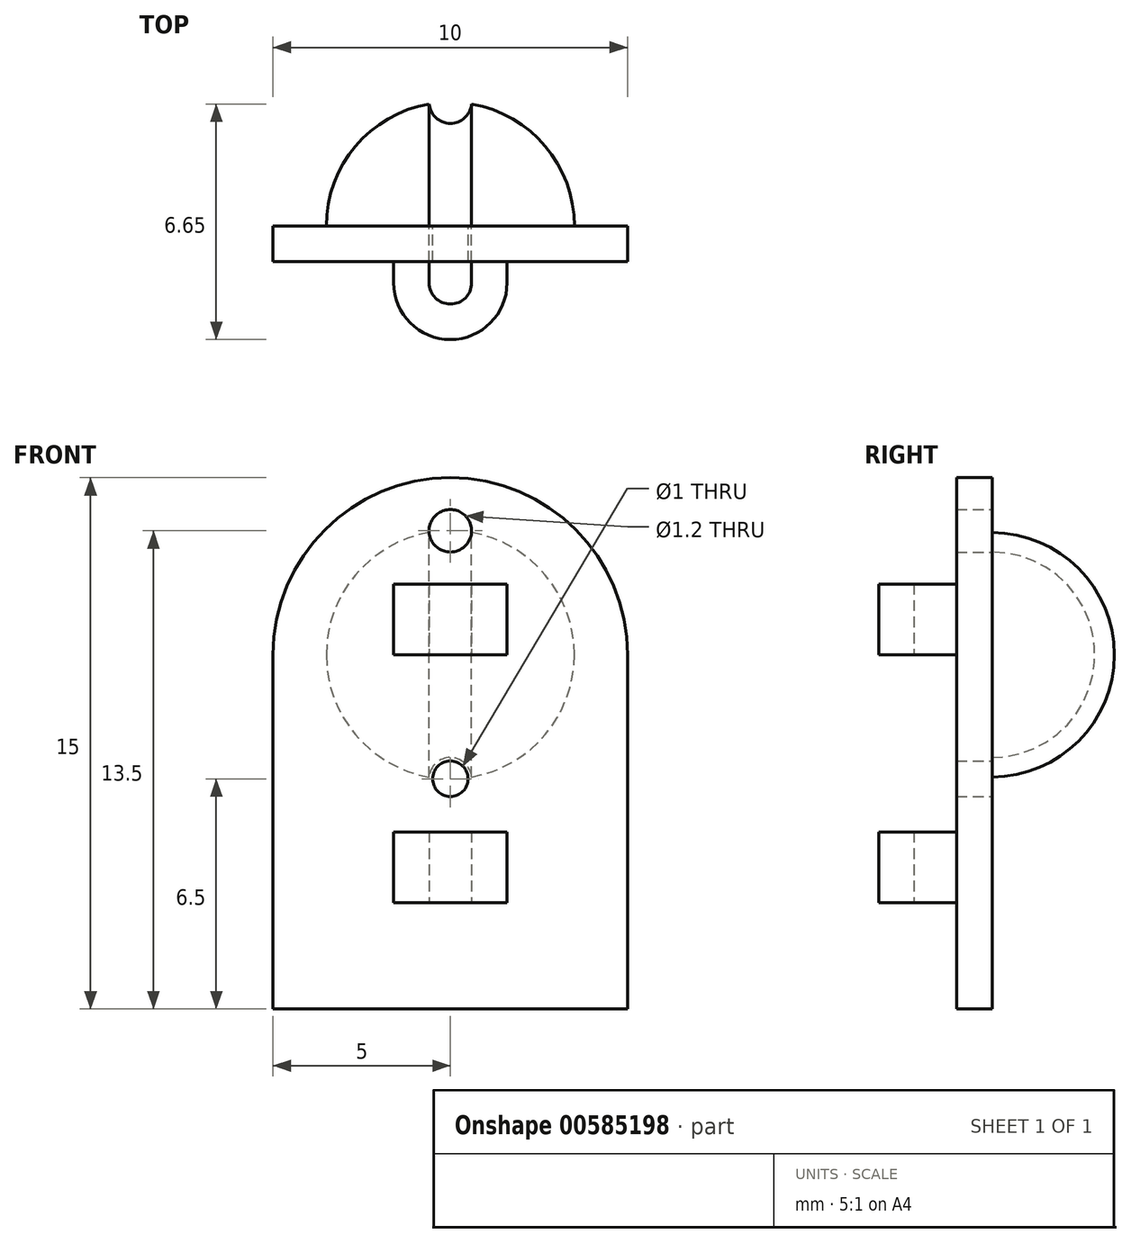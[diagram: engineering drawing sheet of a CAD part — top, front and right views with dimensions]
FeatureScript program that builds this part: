
annotation { "Feature Type Name" : "Feature", "Feature Type Description" : "" }
export const myFeature = defineFeature(function(context is Context, id is Id, definition is map)
    precondition{}
    {
        {
            var Q0;
            Q0=qCreatedBy(makeId("Front.planeOp"),FACE);
            var sketch = newSketch(context, id + "F0", { "sketchPlane" : qUnion([Q0])});
            skCircle(sketch, "E0", {"center": v(0, 10) * mm, "radius": 5 * mm, "construction": true});
            skLineSegment(sketch, "E1", {"start": v(0, 10) * mm, "end": v(-16.65, 10) * mm, "construction": true});
            skLineSegment(sketch, "E2", {"start": v(-16.65, 10) * mm, "end": v(19.24, 10) * mm, "construction": true});
            skLineSegment(sketch, "E3", {"start": v(-5, 10) * mm, "end": v(-5, 0) * mm});
            skLineSegment(sketch, "E4", {"start": v(5, 10) * mm, "end": v(5, 0) * mm});
            skArc(sketch, "E5", {"start": v(5, 10) * mm, "mid": v(0, 15) * mm, "end": v(-5, 10) * mm});
            skCircle(sketch, "E6", {"center": v(0, 10) * mm, "radius": 3.5 * mm, "construction": true});
            skLineSegment(sketch, "E7", {"start": v(-5, 0) * mm, "end": v(5, 0) * mm});
            skLineSegment(sketch, "E8", {"start": v(0, 0) * mm, "end": v(0, 22.5) * mm, "construction": true});
            skCircle(sketch, "E9", {"center": v(0, 13.5) * mm, "radius": 0.6 * mm});
            skCircle(sketch, "E10", {"center": v(0, 6.5) * mm, "radius": 0.5 * mm});
            skArc(sketch, "E11", {"start": v(3.5, 10) * mm, "mid": v(0, 13.5) * mm, "end": v(-3.5, 10) * mm});
            skLineSegment(sketch, "E12", {"start": v(3.5, 10) * mm, "end": v(-3.5, 10) * mm});
            skSolve(sketch);
        }
        {
            var Q0;
            Q0 = qSketchRegion(id + "F0", true);
            var Q1;
            {var subQ0=sQuery(id+"F0.wireOp",EDGE,"E9");var subQ1=sQuery(id+"F0.wireOp",EDGE,"E6");var subQ2=makeQuery(id+"F0.imprint","INTERSECT",VERTEX,{"disambiguationData":[OD(0.0)],"derivedFrom":[subQ1,subQ0]});Q1=makeQuery(id+"F0.imprint","IMPRINT",FACE,{"disambiguationData":[TD([[makeQuery(id+"F0.imprint","IMPRINT",EDGE,{"disambiguationData":[TD([[subQ2,-1.0]])],"derivedFrom":subQ1}),1.0]])]});}
            var Q2;
            {var subQ4=sQuery(id+"F0.wireOp",EDGE,"E12");Q2=makeQuery(id+"F0.imprint","IMPRINT",FACE,{"disambiguationData":[TD([[makeQuery(id+"F0.imprint","IMPRINT",EDGE,{"derivedFrom":subQ4}),-1.0]])]});}
            extrude(context, id + "F1", {"entities" : qUnion([Q0, Q1, Q2]), "depth" : 1 * mm, "offsetDistance" : 25 * mm});
        }
        {
            var Q0;
            {var subQ4=sQuery(id+"F0.wireOp",EDGE,"E12");Q0=makeQuery(id+"F0.imprint","IMPRINT",FACE,{"disambiguationData":[TD([[makeQuery(id+"F0.imprint","IMPRINT",EDGE,{"derivedFrom":subQ4}),-1.0]])]});}
            var Q1;
            Q1=sQuery(id+"F0.wireOp",EDGE,"E2");
            revolve(context, id + "F2", {"operationType" : NewBodyOperationType.ADD, "entities" : qUnion([Q0]), "axis" : qUnion([Q1]), "revolveType" : RevolveType.ONE_DIRECTION, "oppositeDirection" : true, "angle" : 180 * degree});
        }
        {
            var Q0;
            Q0=qCreatedBy(makeId("Top.planeOp"),FACE);
            var sketch = newSketch(context, id + "F3", { "sketchPlane" : qUnion([Q0])});
            skLineSegment(sketch, "E13", {"start": v(0, 0) * mm, "end": v(0, -17.6) * mm, "construction": true});
            skLineSegment(sketch, "E14.top", {"start": v(-1.6, -1.6) * mm, "end": v(1.6, -1.6) * mm});
            skArc(sketch, "E15", {"start": v(-1.6, -1.6) * mm, "mid": v(0, -3.2) * mm, "end": v(1.6, -1.6) * mm});
            skCircle(sketch, "E16", {"center": v(0, -1.6) * mm, "radius": 0.6 * mm, "construction": true});
            skLineSegment(sketch, "E17", {"start": v(0, -1) * mm, "end": v(4.22, -1) * mm, "construction": true});
            skLineSegment(sketch, "E18", {"start": v(4.22, -1) * mm, "end": v(-4.4, -1) * mm, "construction": true});
            skLineSegment(sketch, "E19", {"start": v(-0.6, -1.6) * mm, "end": v(-0.6, -1) * mm});
            skLineSegment(sketch, "E20", {"start": v(0.6, -1.6) * mm, "end": v(0.6, -1) * mm});
            skLineSegment(sketch, "E21", {"start": v(0.6, -1) * mm, "end": v(-0.6, -1) * mm});
            skArc(sketch, "E22", {"start": v(-0.6, -1.6) * mm, "mid": v(0, -2.2) * mm, "end": v(0.6, -1.6) * mm});
            skLineSegment(sketch, "E23", {"start": v(-1.6, -1.6) * mm, "end": v(-1.6, -1) * mm});
            skLineSegment(sketch, "E24", {"start": v(1.6, -1.6) * mm, "end": v(1.6, -1) * mm});
            skLineSegment(sketch, "E25", {"start": v(1.6, -1) * mm, "end": v(-1.6, -1) * mm});
            skSolve(sketch);
        }
        {
            var Q0;
            {var subQ2=sQuery(id+"F3.wireOp",EDGE,"E19");Q0=makeQuery(id+"F3.imprint","IMPRINT",FACE,{"disambiguationData":[TD([[makeQuery(id+"F3.imprint","IMPRINT",EDGE,{"derivedFrom":subQ2}),1.0]])]});}
            var Q1;
            {var subQ0=sQuery(id+"F3.wireOp",EDGE,"E15");Q1=makeQuery(id+"F3.imprint","IMPRINT",FACE,{"disambiguationData":[TD([[makeQuery(id+"F3.imprint","IMPRINT",EDGE,{"derivedFrom":subQ0}),1.0]])]});}
            var Q2;
            {var subQ2=sQuery(id+"F3.wireOp",EDGE,"E20");Q2=makeQuery(id+"F3.imprint","IMPRINT",FACE,{"disambiguationData":[TD([[makeQuery(id+"F3.imprint","IMPRINT",EDGE,{"derivedFrom":subQ2}),-1.0]])]});}
            extrude(context, id + "F4", {"entities" : qUnion([Q0, Q1, Q2]), "operationType" : NewBodyOperationType.ADD, "depth" : 12 * mm, "offsetDistance" : 25 * mm});
        }
        {
            var Q0;
            Q0=qCreatedBy(makeId("Right.planeOp"),FACE);
            var sketch = newSketch(context, id + "F5", { "sketchPlane" : qUnion([Q0])});
            skLineSegment(sketch, "E26", {"start": v(-1, 0) * mm, "end": v(-1, 23.03) * mm, "construction": true});
            skLineSegment(sketch, "E27", {"start": v(-1, 5) * mm, "end": v(-13.93, 5) * mm, "construction": true});
            skLineSegment(sketch, "E28", {"start": v(-1, 10) * mm, "end": v(-13.8, 10) * mm, "construction": true});
            skLineSegment(sketch, "E29", {"start": v(-1, 3) * mm, "end": v(-13.94, 3) * mm, "construction": true});
            skLineSegment(sketch, "E30", {"start": v(-6, 0) * mm, "end": v(-6, 23.26) * mm, "construction": true});
            skLineSegment(sketch, "E31.bottom", {"start": v(-6, 10) * mm, "end": v(-1, 10) * mm});
            skLineSegment(sketch, "E31.top", {"start": v(-6, 5) * mm, "end": v(-1, 5) * mm});
            skLineSegment(sketch, "E31.left", {"start": v(-6, 10) * mm, "end": v(-6, 5) * mm});
            skLineSegment(sketch, "E31.right", {"start": v(-1, 10) * mm, "end": v(-1, 5) * mm});
            skLineSegment(sketch, "E32.bottom", {"start": v(-6, 3) * mm, "end": v(-1, 3) * mm});
            skLineSegment(sketch, "E32.top", {"start": v(-6, 0) * mm, "end": v(-1, 0) * mm});
            skLineSegment(sketch, "E32.left", {"start": v(-6, 3) * mm, "end": v(-6, 0) * mm});
            skLineSegment(sketch, "E32.right", {"start": v(-1, 3) * mm, "end": v(-1, 0) * mm});
            skSolve(sketch);
        }
        {
            var Q0;
            Q0=makeQuery(id+"F5.imprint","IMPRINT",FACE,{"disambiguationData":[TD([[makeQuery(id+"F5.imprint","IMPRINT",EDGE,{"derivedFrom":sQuery(id+"F5.wireOp",EDGE,"E31.bottom")}),-1.0]])]});
            var Q1;
            Q1=makeQuery(id+"F5.imprint","IMPRINT",FACE,{"disambiguationData":[TD([[makeQuery(id+"F5.imprint","IMPRINT",EDGE,{"derivedFrom":sQuery(id+"F5.wireOp",EDGE,"E32.bottom")}),-1.0]])]});
            extrude(context, id + "F6", {"entities" : qUnion([Q0, Q1]), "operationType" : NewBodyOperationType.REMOVE, "oppositeDirection" : true, "depth" : 25 * mm, "offsetDistance" : 25 * mm});
        }
        {
            var Q0;
            Q0=makeQuery(id+"F5.imprint","IMPRINT",FACE,{"disambiguationData":[TD([[makeQuery(id+"F5.imprint","IMPRINT",EDGE,{"derivedFrom":sQuery(id+"F5.wireOp",EDGE,"E31.bottom")}),-1.0]])]});
            var Q1;
            Q1=makeQuery(id+"F5.imprint","IMPRINT",FACE,{"disambiguationData":[TD([[makeQuery(id+"F5.imprint","IMPRINT",EDGE,{"derivedFrom":sQuery(id+"F5.wireOp",EDGE,"E32.bottom")}),-1.0]])]});
            extrude(context, id + "F7", {"entities" : qUnion([Q0, Q1]), "operationType" : NewBodyOperationType.REMOVE, "depth" : 25 * mm, "offsetDistance" : 25 * mm});
        }
    });
